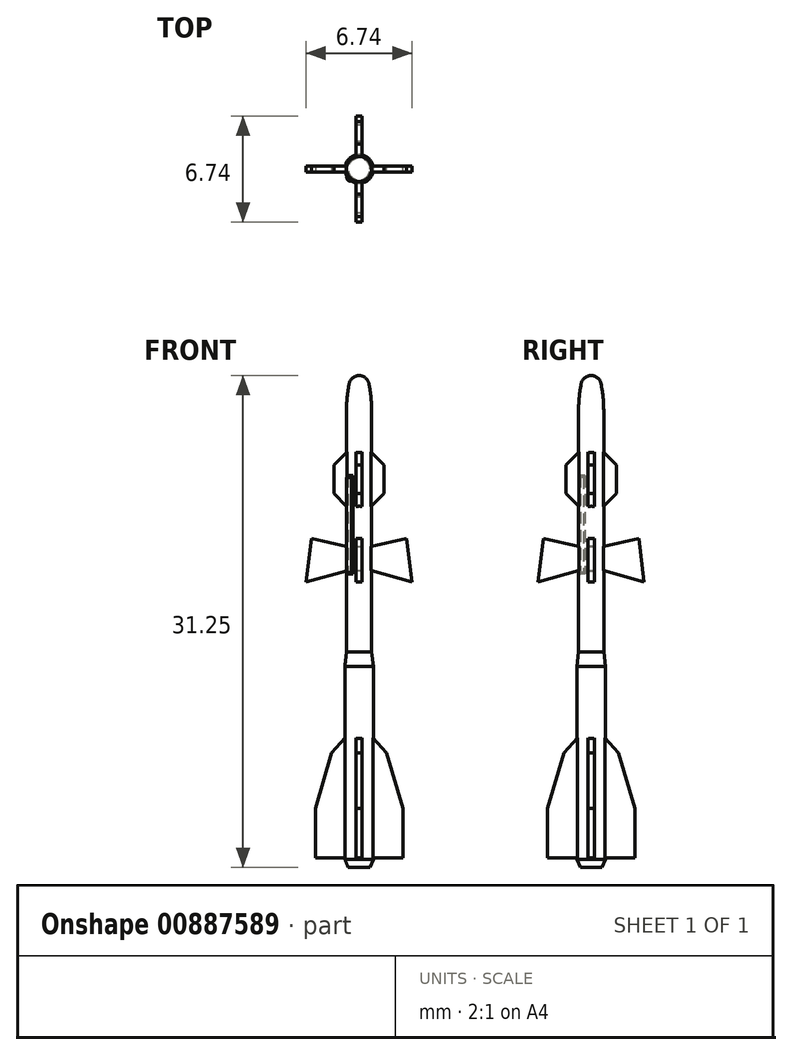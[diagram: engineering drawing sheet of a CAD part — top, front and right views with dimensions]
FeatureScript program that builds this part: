
annotation { "Feature Type Name" : "Feature", "Feature Type Description" : "" }
export const myFeature = defineFeature(function(context is Context, id is Id, definition is map)
    precondition{}
    {
        {
            assignVariable(context, id + "F0", {"name" : "s", "anyValue" : 144});
        }
        {
            var Q0;
            Q0=qCreatedBy(makeId("Front.planeOp"),FACE);
            var sketch = newSketch(context, id + "F1", { "sketchPlane" : qUnion([Q0])});
            skLineSegment(sketch, "E0", {"start": v(0, 0) * mm, "end": v(0, 31.25) * mm});
            skLineSegment(sketch, "E1", {"start": v(0.8, 29) * mm, "end": v(0.8, 0) * mm});
            skLineSegment(sketch, "E2", {"start": v(0.8, 0) * mm, "end": v(0, 0) * mm});
            skArc(sketch, "E3", {"start": v(0.63, 30.73) * mm, "mid": v(0.4, 31.1) * mm, "end": v(0, 31.25) * mm});
            skLineSegment(sketch, "E4", {"start": v(0, 31.25) * mm, "end": v(2.5, 31.25) * mm, "construction": true});
            skArc(sketch, "E5", {"start": v(0.8, 29) * mm, "mid": v(0.76, 29.87) * mm, "end": v(0.63, 30.73) * mm});
            skLineSegment(sketch, "E6", {"start": v(0.8, 13.68) * mm, "end": v(0.9, 12.78) * mm});
            skLineSegment(sketch, "E7", {"start": v(0.9, 12.78) * mm, "end": v(0.9, 0) * mm});
            skLineSegment(sketch, "E8", {"start": v(0.9, 0) * mm, "end": v(0.8, 0) * mm});
            skLineSegment(sketch, "E9", {"start": v(0.7, 0) * mm, "end": v(0.9, 0.52) * mm});
            skSolve(sketch);
        }
        {
            var Q0;
            {var subQ0=sQuery(id+"F1.wireOp",EDGE,"E6");Q0=makeQuery(id+"F1.imprint","IMPRINT",FACE,{"disambiguationData":[TD([[makeQuery(id+"F1.imprint","IMPRINT",EDGE,{"derivedFrom":subQ0}),-1.0]])]});}
            var Q1;
            {var subQ7=sQuery(id+"F1.wireOp",EDGE,"E0");Q1=makeQuery(id+"F1.imprint","IMPRINT",FACE,{"disambiguationData":[TD([[makeQuery(id+"F1.imprint","IMPRINT",EDGE,{"derivedFrom":subQ7}),-1.0]])]});}
            var Q2;
            Q2=sQuery(id+"F1.wireOp",EDGE,"E0");
            revolve(context, id + "F2", {"surfaceOperationType" : NewSurfaceOperationType.NEW, "entities" : qUnion([Q0, Q1]), "axis" : qUnion([Q2]), "revolveType" : RevolveType.FULL});
        }
        {
            var Q0;
            Q0=qCreatedBy(makeId("Front.planeOp"),FACE);
            var sketch = newSketch(context, id + "F3", { "sketchPlane" : qUnion([Q0])});
            skLineSegment(sketch, "E10", {"start": v(0, 0) * mm, "end": v(0, 27.15) * mm});
            skLineSegment(sketch, "E11", {"start": v(0, 27.15) * mm, "end": v(1.6, 25.56) * mm});
            skLineSegment(sketch, "E12", {"start": v(1.6, 25.56) * mm, "end": v(1.6, 23.75) * mm});
            skLineSegment(sketch, "E13", {"start": v(1.6, 23.75) * mm, "end": v(0.4, 22.55) * mm});
            skLineSegment(sketch, "E14", {"start": v(0.4, 22.55) * mm, "end": v(0.4, 20.3) * mm});
            skLineSegment(sketch, "E15", {"start": v(0.4, 20.3) * mm, "end": v(3.02, 20.9) * mm});
            skLineSegment(sketch, "E16", {"start": v(3.02, 20.9) * mm, "end": v(3.37, 18.12) * mm});
            skLineSegment(sketch, "E17", {"start": v(3.37, 18.13) * mm, "end": v(0.4, 18.96) * mm});
            skLineSegment(sketch, "E18", {"start": v(0.4, 18.96) * mm, "end": v(0.4, 8.74) * mm});
            skLineSegment(sketch, "E19", {"start": v(0.4, 8.74) * mm, "end": v(1.74, 7.3) * mm});
            skLineSegment(sketch, "E20", {"start": v(1.74, 7.3) * mm, "end": v(2.78, 3.75) * mm});
            skLineSegment(sketch, "E21", {"start": v(2.78, 3.75) * mm, "end": v(2.78, 0.63) * mm});
            skLineSegment(sketch, "E22", {"start": v(0.9, 0) * mm, "end": v(0.9, 32.87) * mm, "construction": true});
            skPoint(sketch, "E23", {"position": v(0.9, 8.2) * mm});
            skPoint(sketch, "E24", {"position": v(0.9, 18.82) * mm});
            skPoint(sketch, "E25", {"position": v(0.9, 20.42) * mm});
            skPoint(sketch, "E26", {"position": v(0.9, 23.06) * mm});
            skPoint(sketch, "E27", {"position": v(0.9, 26.25) * mm});
            skLineSegment(sketch, "E28", {"start": v(2.78, 0.63) * mm, "end": v(0, 0.63) * mm});
            skLineSegment(sketch, "E29.0", {"start": v(0.9, 0.52) * mm, "end": v(-0.9, 0.52) * mm});
            skSolve(sketch);
        }
        {
            var Q0;
            Q0=qSketchRegion(id+"F3",true);
            extrude(context, id + "F4", {"entities" : qUnion([Q0]), "operationType" : NewBodyOperationType.ADD, "depth" : .4 * mm, "offsetDistance" : 25 * mm, "symmetric" : true});
        }
        {
            var Q0;
            Q0=makeQuery(id+"F2.opRevolve","SWEPT_BODY",BODY,{"disambiguationData":[OSD([sQuery(id+"F1.wireOp",EDGE,"E0"),sQuery(id+"F1.wireOp",EDGE,"E1"),sQuery(id+"F1.wireOp",EDGE,"E2"),sQuery(id+"F1.wireOp",EDGE,"E3"),sQuery(id+"F1.wireOp",EDGE,"E5")])]});
            var Q1;
            Q1=makeQuery(id+"F2.opRevolve","SWEPT_FACE",FACE,{"disambiguationData":[OSD([sQuery(id+"F1.wireOp",EDGE,"E1")])]});
            circularPattern(context, id + "F5", {"operationType" : NewBodyOperationType.ADD, "entities" : qUnion([Q0]), "axis" : qUnion([Q1]), "angle" : 360 * degree, "instanceCount" : 4, "equalSpace" : true, "computeTransformsWithoutBuiltin" : true});
        }
        {
            var Q0;
            Q0=qCreatedBy(makeId("Top.planeOp"),FACE);
            cPlane(context, id + "F6", {"entities" : qUnion([Q0]), "cplaneType" : CPlaneType.OFFSET, "offset" : (2700 / getVariable(context, 's')) * mm, "width" : 150 * mm, "height" : 150 * mm});
        }
        {
            var Q0;
            Q0=qCreatedBy(id+"F6.planeOp",FACE);
            var sketch = newSketch(context, id + "F7", { "sketchPlane" : qUnion([Q0])});
            skLineSegment(sketch, "E30", {"start": v(-0.08, -0.37) * mm, "end": v(-0.37, -0.08) * mm});
            skLineSegment(sketch, "E31", {"start": v(-0.37, -0.08) * mm, "end": v(-0.78, -0.48) * mm});
            skLineSegment(sketch, "E32", {"start": v(-0.48, -0.78) * mm, "end": v(-0.08, -0.37) * mm});
            skLineSegment(sketch, "E33", {"start": v(0, -0.64) * mm, "end": v(0, 0) * mm, "construction": true});
            skLineSegment(sketch, "E34", {"start": v(0, 0) * mm, "end": v(-0.22, -0.22) * mm, "construction": true});
            skArc(sketch, "E35", {"start": v(-0.78, -0.48) * mm, "mid": v(-0.7, -0.7) * mm, "end": v(-0.48, -0.78) * mm});
            skSolve(sketch);
        }
        {
            var Q0;
            Q0=qSketchRegion(id+"F7",true);
            extrude(context, id + "F8", {"entities" : qUnion([Q0]), "operationType" : NewBodyOperationType.ADD, "depth" : (870 / getVariable(context, 's')) * mm, "offsetDistance" : 25 * mm});
        }
        {
            var Q0;
            Q0=makeQuery(id+"F8.boolean.opBoolean","INTERSECT",EDGE,{"derivedFrom":[makeQuery(id+"F2.opRevolve","SWEPT_FACE",FACE,{"disambiguationData":[OSD([sQuery(id+"F1.wireOp",EDGE,"E1")])]}),makeQuery(id+"F8.opExtrude","CAP_FACE",FACE,{"disambiguationData":[OSD([sQuery(id+"F7.wireOp",EDGE,"E30"),sQuery(id+"F7.wireOp",EDGE,"E31"),sQuery(id+"F7.wireOp",EDGE,"E32"),sQuery(id+"F7.wireOp",EDGE,"E35")])],"isStart":false})]});
            var Q1;
            Q1=makeQuery(id+"F8.boolean.opBoolean","INTERSECT",EDGE,{"derivedFrom":[makeQuery(id+"F2.opRevolve","SWEPT_FACE",FACE,{"disambiguationData":[OSD([sQuery(id+"F1.wireOp",EDGE,"E1")])]}),makeQuery(id+"F8.opExtrude","CAP_FACE",FACE,{"disambiguationData":[OSD([sQuery(id+"F7.wireOp",EDGE,"E30"),sQuery(id+"F7.wireOp",EDGE,"E31"),sQuery(id+"F7.wireOp",EDGE,"E32"),sQuery(id+"F7.wireOp",EDGE,"E35")])],"isStart":true})]});
            chamfer(context, id + "F9", {"entities" : qUnion([Q0, Q1]), "width" : .1 * mm, "tangentPropagation" : true});
        }
    });
